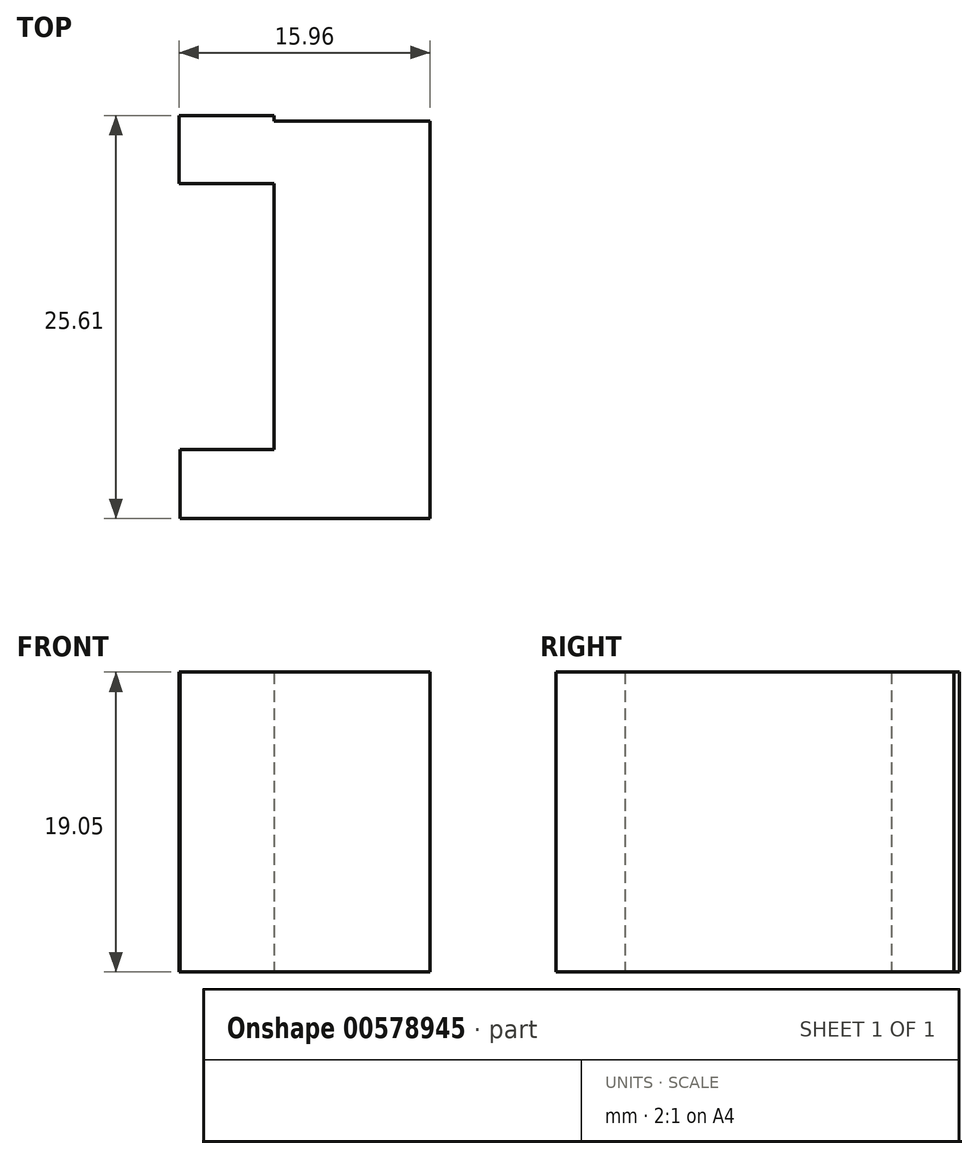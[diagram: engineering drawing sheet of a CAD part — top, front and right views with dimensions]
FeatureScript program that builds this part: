
annotation { "Feature Type Name" : "Feature", "Feature Type Description" : "" }
export const myFeature = defineFeature(function(context is Context, id is Id, definition is map)
    precondition{}
    {
        {
            var Q0;
            Q0=qCreatedBy(makeId("Top.planeOp"),FACE);
            var sketch = newSketch(context, id + "F0", { "sketchPlane" : qUnion([Q0])});
            skLineSegment(sketch, "E0", {"start": v(31.91, 33.86) * mm, "end": v(31.91, 27.44) * mm});
            skLineSegment(sketch, "E1", {"start": v(31.91, 27.44) * mm, "end": v(38.34, 27.44) * mm});
            skLineSegment(sketch, "E2", {"start": v(38.34, 27.44) * mm, "end": v(38.34, 12.74) * mm});
            skLineSegment(sketch, "E3", {"start": v(38.34, 12.74) * mm, "end": v(31.91, 12.74) * mm});
            skLineSegment(sketch, "E4", {"start": v(31.91, 12.74) * mm, "end": v(31.91, 6.31) * mm});
            skLineSegment(sketch, "E5", {"start": v(31.91, 6.31) * mm, "end": v(48.94, 6.31) * mm});
            skLineSegment(sketch, "E6", {"start": v(48.94, 6.31) * mm, "end": v(48.94, 33.86) * mm});
            skLineSegment(sketch, "E7", {"start": v(48.94, 33.86) * mm, "end": v(31.91, 33.86) * mm});
            skSolve(sketch);
        }
        {
            var Q0;
            Q0=sQuery(id+"F0.wireOp",EDGE,"E7");
            var Q1;
            Q1=sQuery(id+"F0.wireOp",EDGE,"E4");
            var Q2;
            Q2=sQuery(id+"F0.wireOp",EDGE,"E1");
            var Q3;
            Q3=sQuery(id+"F0.wireOp",EDGE,"E2");
            var Q4;
            Q4=sQuery(id+"F0.wireOp",EDGE,"E0");
            var Q5;
            Q5=sQuery(id+"F0.wireOp",EDGE,"E5");
            var Q6;
            Q6=sQuery(id+"F0.wireOp",EDGE,"E3");
            var Q7;
            Q7=sQuery(id+"F0.wireOp",EDGE,"E6");
            extrude(context, id + "F1", {"bodyType" : ToolBodyType.SURFACE, "surfaceEntities" : qUnion([Q0, Q1, Q2, Q3, Q4, Q5, Q6, Q7]), "depth" : 20.32 * mm, "offsetDistance" : 25.4 * mm});
        }
        {
            var Q0;
            Q0=qCreatedBy(makeId("Top.planeOp"),FACE);
            var sketch = newSketch(context, id + "F2", { "sketchPlane" : qUnion([Q0])});
            skLineSegment(sketch, "E8.bottom", {"start": v(38.85, 33.43) * mm, "end": v(48.76, 33.43) * mm});
            skLineSegment(sketch, "E8.top", {"start": v(38.85, 8.18) * mm, "end": v(48.76, 8.18) * mm});
            skLineSegment(sketch, "E8.left", {"start": v(38.85, 33.43) * mm, "end": v(38.85, 8.18) * mm});
            skLineSegment(sketch, "E8.right", {"start": v(48.76, 33.43) * mm, "end": v(48.76, 8.18) * mm});
            skLineSegment(sketch, "E9.bottom", {"start": v(32.9, 12.57) * mm, "end": v(38.85, 12.57) * mm});
            skLineSegment(sketch, "E9.top", {"start": v(32.9, 8.18) * mm, "end": v(38.85, 8.18) * mm});
            skLineSegment(sketch, "E9.left", {"start": v(32.9, 12.57) * mm, "end": v(32.9, 8.18) * mm});
            skLineSegment(sketch, "E9.right", {"start": v(38.85, 12.57) * mm, "end": v(38.85, 8.18) * mm});
            skLineSegment(sketch, "E10.bottom", {"start": v(32.8, 33.8) * mm, "end": v(38.85, 33.8) * mm});
            skLineSegment(sketch, "E10.top", {"start": v(32.8, 29.46) * mm, "end": v(38.85, 29.46) * mm});
            skLineSegment(sketch, "E10.left", {"start": v(32.8, 33.8) * mm, "end": v(32.8, 29.46) * mm});
            skLineSegment(sketch, "E10.right", {"start": v(38.85, 33.8) * mm, "end": v(38.85, 29.46) * mm});
            skSolve(sketch);
        }
        {
            var Q0;
            Q0 = qSketchRegion(id + "F2", true);
            extrude(context, id + "F3", {"entities" : qUnion([Q0]), "depth" : 19.05 * mm, "offsetDistance" : 25.4 * mm});
        }
    });
